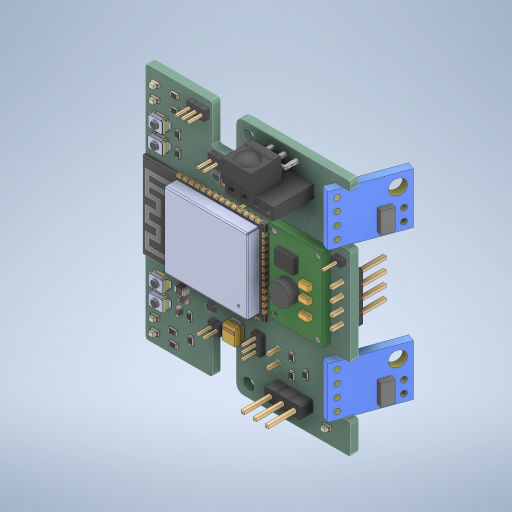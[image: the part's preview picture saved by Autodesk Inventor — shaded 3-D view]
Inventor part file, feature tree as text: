
AUTODESK INVENTOR PART (.ipt)
format: ipt  version: 2023.5 (Build 275446000, 446)  size: 2,956,800 bytes
history: native  units: mm
features: other x126, extrude x1, sketch x1, projected_geometry x1
ambient origin geometry x8: Origin, YZ Plane, XZ Plane, XY Plane, X Axis, Y Axis, Z Axis, Center Point
bodies: Body1 (feature_tree), Body2 (feature_tree), Body3 (feature_tree), Body4 (feature_tree), Body5 (feature_tree), Body6 (feature_tree), Body7 (feature_tree), Body8 (feature_tree), Body9 (feature_tree), Body10 (feature_tree), Body11 (feature_tree), Body12 (feature_tree), Body13 (feature_tree), Body14 (feature_tree), Body15 (feature_tree), Body16 (feature_tree), Body17 (feature_tree), Body18 (feature_tree), Body19 (feature_tree), Body20 (feature_tree), Body21 (feature_tree), Body22 (feature_tree), Body23 (feature_tree), Body24 (feature_tree), Body25 (feature_tree), Body26 (feature_tree), Body27 (feature_tree), Body28 (feature_tree), Body29 (feature_tree), Body30 (feature_tree), Body31 (feature_tree), Body32 (feature_tree), Body33 (feature_tree), Body34 (feature_tree), Body35 (feature_tree), Body36 (feature_tree), Body37 (feature_tree), Body38 (feature_tree), Body39 (feature_tree), Body40 (feature_tree), Body41 (feature_tree), Body42 (feature_tree), Body43 (feature_tree), Body44 (feature_tree), Body45 (feature_tree), Body46 (feature_tree), Body47 (feature_tree), Body48 (feature_tree), Body49 (feature_tree), Body50 (feature_tree), Body51 (feature_tree), Body52 (feature_tree), Body53 (feature_tree), Body54 (feature_tree), Body55 (feature_tree), Body56 (feature_tree), Body57 (feature_tree), Body58 (feature_tree), Body59 (feature_tree), Body60 (feature_tree), Body61 (feature_tree), Body62 (feature_tree), Body63 (feature_tree), Body64 (feature_tree), Body65 (feature_tree), Body66 (feature_tree), Body67 (feature_tree), Body68 (feature_tree), Body69 (feature_tree), Body70 (feature_tree), Body71 (feature_tree), Body72 (feature_tree), Body73 (feature_tree), Body74 (feature_tree), Body75 (feature_tree), Body76 (feature_tree), Body77 (feature_tree), Body78 (feature_tree), Body79 (feature_tree), Body80 (feature_tree), Body81 (feature_tree), Body82 (feature_tree), Body83 (feature_tree), Body84 (feature_tree), Body85 (feature_tree), Body86 (feature_tree), Body87 (feature_tree), Body88 (feature_tree), Body89 (feature_tree), Body90 (feature_tree), Body91 (feature_tree), Body92 (feature_tree), Body93 (feature_tree), Body94 (feature_tree), Body95 (feature_tree), Body96 (feature_tree), Body97 (feature_tree), Body98 (feature_tree), Body99 (feature_tree), Body100 (feature_tree), Body101 (feature_tree), Body102 (feature_tree), Body103 (feature_tree), Body104 (feature_tree), Body105 (feature_tree), Body106 (feature_tree), Body107 (feature_tree), Body108 (feature_tree), Body109 (feature_tree), Body110 (feature_tree), Body111 (feature_tree), Body112 (feature_tree), Body113 (feature_tree), Body114 (feature_tree), Body115 (feature_tree), Body116 (feature_tree), Body117 (feature_tree), Body118 (feature_tree), Body119 (feature_tree), Body120 (feature_tree), Body121 (feature_tree), Body122 (feature_tree), Body123 (feature_tree), Body124 (feature_tree), Body125 (feature_tree), Body126 (feature_tree)
feature tree (129):
  other  "Bryła1"
  extrude  "Wyciągnięcie proste1"  Depth=1.1mm TaperAngle=0.0deg
  other  "Bryła2"
  other  "Bryła3"
  other  "Bryła4"
  other  "Bryła5"
  other  "Bryła6"
  other  "Bryła7"
  other  "Bryła8"
  other  "Bryła9"
  other  "Bryła10"
  other  "Bryła11"
  other  "Bryła12"
  other  "Bryła13"
  other  "Bryła14"
  other  "Bryła15"
  other  "Bryła16"
  other  "Bryła17"
  other  "Bryła18"
  other  "Bryła19"
  other  "Bryła20"
  other  "Bryła21"
  other  "Bryła22"
  other  "Bryła23"
  other  "Bryła24"
  other  "Bryła25"
  other  "Bryła26"
  other  "Bryła27"
  other  "Bryła28"
  other  "Bryła29"
  other  "Bryła30"
  other  "Bryła31"
  other  "Bryła32"
  other  "Bryła33"
  other  "Bryła34"
  other  "Bryła35"
  other  "Bryła36"
  other  "Bryła37"
  other  "Bryła38"
  other  "Bryła39"
  other  "Bryła40"
  other  "Bryła41"
  other  "Bryła42"
  other  "Bryła43"
  other  "Bryła44"
  other  "Bryła45"
  other  "Bryła46"
  other  "Bryła47"
  other  "Bryła48"
  other  "Bryła49"
  other  "Bryła50"
  other  "Bryła51"
  other  "Bryła52"
  other  "Bryła53"
  other  "Bryła54"
  other  "Bryła55"
  other  "Bryła56"
  other  "Bryła57"
  other  "Bryła58"
  other  "Bryła59"
  other  "Bryła60"
  other  "Bryła61"
  other  "Bryła62"
  other  "Bryła63"
  other  "Bryła64"
  other  "Bryła65"
  other  "Bryła66"
  other  "Bryła67"
  other  "Bryła68"
  other  "Bryła69"
  other  "Bryła70"
  other  "Bryła71"
  other  "Bryła72"
  other  "Bryła73"
  other  "Bryła74"
  other  "Bryła75"
  other  "Bryła76"
  other  "Bryła77"
  other  "Bryła78"
  other  "Bryła79"
  other  "Bryła80"
  other  "Bryła81"
  other  "Bryła82"
  other  "Bryła83"
  other  "Bryła84"
  other  "Bryła85"
  other  "Bryła86"
  other  "Bryła87"
  other  "Bryła88"
  other  "Bryła89"
  other  "Bryła90"
  other  "Bryła91"
  other  "Bryła92"
  other  "Bryła93"
  other  "Bryła94"
  other  "Bryła95"
  other  "Bryła96"
  other  "Bryła97"
  other  "Bryła98"
  other  "Bryła99"
  other  "Bryła100"
  other  "Bryła101"
  other  "Bryła102"
  other  "Bryła103"
  other  "Bryła104"
  other  "Bryła105"
  other  "Bryła106"
  other  "Bryła107"
  other  "Bryła108"
  other  "Bryła109"
  other  "Bryła110"
  other  "Bryła111"
  other  "Bryła112"
  other  "Bryła113"
  other  "Bryła114"
  other  "Bryła115"
  other  "Bryła116"
  other  "Bryła117"
  other  "Bryła118"
  other  "Bryła119"
  other  "Bryła120"
  other  "Bryła121"
  other  "Bryła122"
  other  "Bryła123"
  other  "Bryła124"
  other  "Bryła125"
  other  "Bryła126"
  sketch  "Szkic1"
  projected_geometry  "Pętla rzutowana1"
